# Revit family: Kombiprofilhalter, fvz
name_source: partatom
category: HLS-Bauteile
units: mm (PartAtom-declared; Revit-internal decimal feet)

## family parameters
Arbeitsebenenbasiert = Ja
Beim Laden mit Abzugskörper schneiden = Nein
Bemaßung runder Anschluss = Durchmesser verwenden
Beschriftungsausrichtung beibehalten = Nein
Gemeinsam genutzt = Ja
Immer vertikal = Nein
Raumberechnungspunkt = Nein
Teiletyp = Normal

## types (3) — shared parameters
Breite = 43 mm
Fabrikat = MEFA
Gewicht = 0.05 kg
Gewicht pro Bauteil = 0.05 kg
Höhe = 10.1 mm
Klauenbreite 1 = 21 mm
Klauenbreite 2 = 16 mm
Kurztext1 = Kombiprofilhalter fvz
Länge = 52 mm
Material = Stahl
Materialname = S235
Mengeneinheit = St
Profiltyp = 35, 45, Stex 35
Stärke Material = 3 mm  [stored 0.00984252 ft]
Vorgabe-Ansicht = 1219 mm
max. zul. Last = 4.70 kN
vpe = 100

## per-type parameters (varying)
| type | Artikelnummer | D | EAN | Kurztext2 | Lochdurchmesser | für Gewinde |
| Kombiprofilhalter 11, fvz | 08095035/fvz | 11 mm | 4250928459466 | Bohrung 11 mm für Gewinde M10 | 11 mm | M10 |
| Kombiprofilhalter 13, fvz | 08162945/fvz | 13 mm | 4250928459657 | Bohrung 13 mm für Gewinde M12 | 13 mm | M12 |
| Kombiprofilhalter 17, fvz | 08163365/fvz | 17 mm | 4250928459473 | Bohrung 17 mm für Gewinde M16 | 17 mm | M16 |

note: [stored X ft] marks values corroborated as IEEE doubles in the binary element streams (Revit-internal decimal feet)
